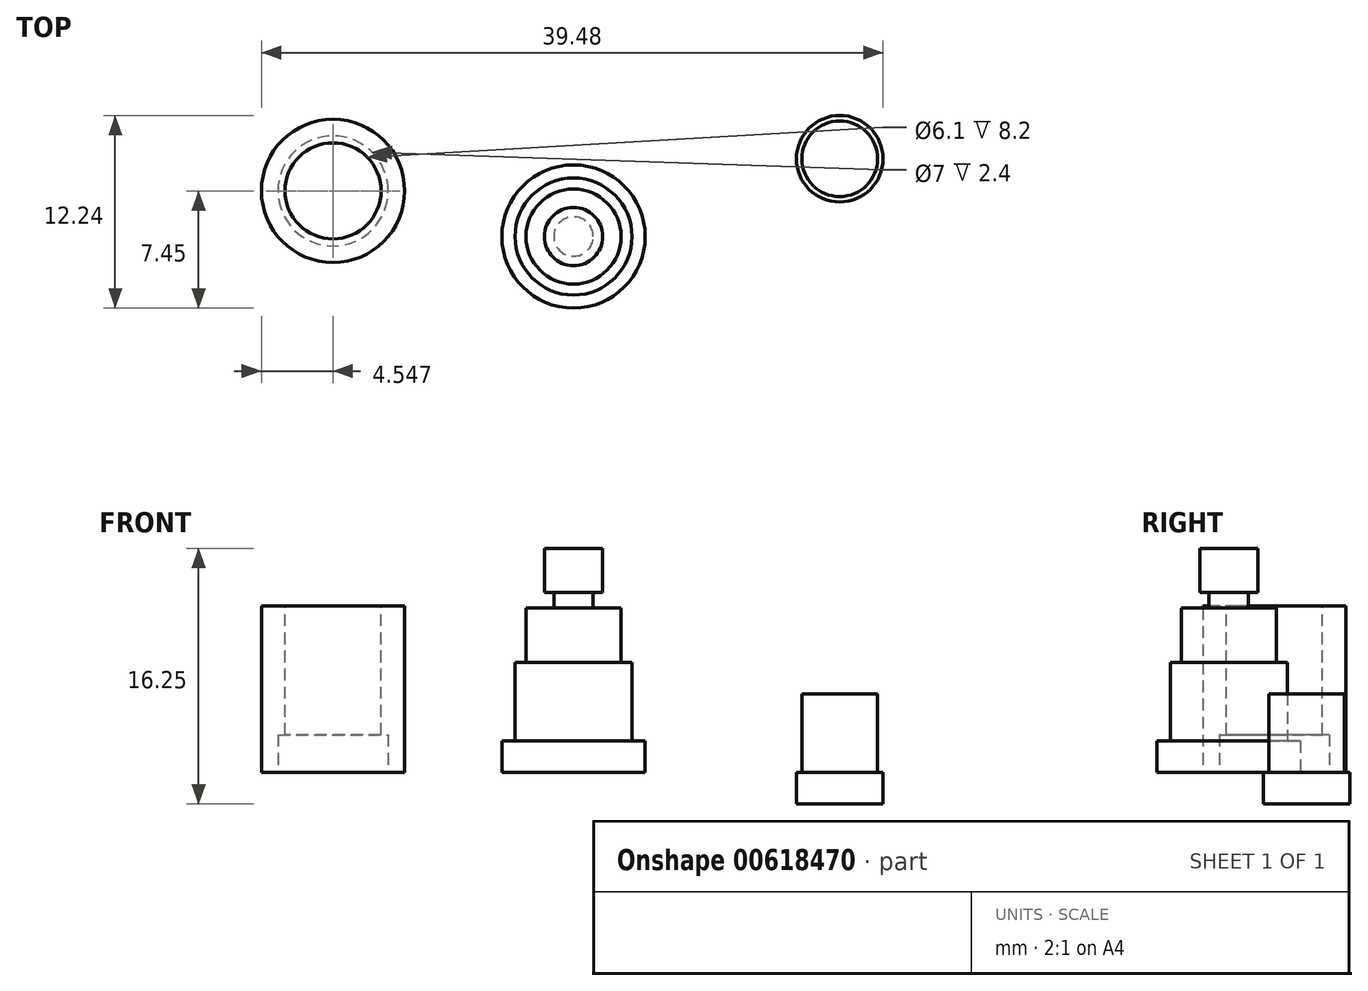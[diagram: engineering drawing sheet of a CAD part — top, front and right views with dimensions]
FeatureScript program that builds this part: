
annotation { "Feature Type Name" : "Feature", "Feature Type Description" : "" }
export const myFeature = defineFeature(function(context is Context, id is Id, definition is map)
    precondition{}
    {
        {
            var Q0;
            Q0=qCreatedBy(makeId("Top.planeOp"),FACE);
            var sketch = newSketch(context, id + "F0", { "sketchPlane" : qUnion([Q0])});
            skCircle(sketch, "E0", {"center": v(0, 0) * mm, "radius": 4.55 * mm});
            skSolve(sketch);
        }
        {
            var Q0;
            Q0=qCreatedBy(makeId("Top.planeOp"),FACE);
            var sketch = newSketch(context, id + "F1", { "sketchPlane" : qUnion([Q0])});
            skCircle(sketch, "E1", {"center": v(-15.27, 2.9) * mm, "radius": 4.55 * mm});
            skSolve(sketch);
        }
        {
            var Q0;
            Q0 = qSketchRegion(id + "F0", true);
            extrude(context, id + "F2", {"entities" : qUnion([Q0]), "depth" : 2 * mm, "offsetDistance" : 25 * mm});
        }
        {
            var Q0;
            Q0=makeQuery(id+"F2.opExtrude","CAP_FACE",FACE,{"disambiguationData":[OSD([sQuery(id+"F0.wireOp",EDGE,"E0")])],"isStart":false});
            var sketch = newSketch(context, id + "F3", { "sketchPlane" : qUnion([Q0])});
            skCircle(sketch, "E2", {"center": v(0, 0) * mm, "radius": 3.71 * mm});
            skSolve(sketch);
        }
        {
            var Q0;
            Q0=makeQuery(id+"F3.imprint","IMPRINT",FACE,{"disambiguationData":[TD([[makeQuery(id+"F3.imprint","IMPRINT",EDGE,{"derivedFrom":sQuery(id+"F3.wireOp",EDGE,"E2")}),1.0]])]});
            extrude(context, id + "F4", {"entities" : qUnion([Q0]), "operationType" : NewBodyOperationType.ADD, "depth" : 5 * mm, "offsetDistance" : 25 * mm});
        }
        {
            var Q0;
            Q0=makeQuery(id+"F4.opExtrude","CAP_FACE",FACE,{"disambiguationData":[OSD([sQuery(id+"F3.wireOp",EDGE,"E2")])],"isStart":false});
            var sketch = newSketch(context, id + "F5", { "sketchPlane" : qUnion([Q0])});
            skCircle(sketch, "E3", {"center": v(0, 0) * mm, "radius": 3.02 * mm});
            skSolve(sketch);
        }
        {
            var Q0;
            Q0=makeQuery(id+"F5.imprint","IMPRINT",FACE,{"disambiguationData":[TD([[makeQuery(id+"F5.imprint","IMPRINT",EDGE,{"derivedFrom":sQuery(id+"F5.wireOp",EDGE,"E3")}),1.0]])]});
            extrude(context, id + "F6", {"entities" : qUnion([Q0]), "operationType" : NewBodyOperationType.ADD, "depth" : 3.45 * mm, "offsetDistance" : 25 * mm});
        }
        {
            var Q0;
            Q0=makeQuery(id+"F6.opExtrude","CAP_FACE",FACE,{"disambiguationData":[OSD([sQuery(id+"F5.wireOp",EDGE,"E3")])],"isStart":false});
            var sketch = newSketch(context, id + "F7", { "sketchPlane" : qUnion([Q0])});
            skCircle(sketch, "E4", {"center": v(0, 0) * mm, "radius": 1.25 * mm});
            skSolve(sketch);
        }
        {
            var Q0;
            Q0=makeQuery(id+"F7.imprint","IMPRINT",FACE,{"disambiguationData":[TD([[makeQuery(id+"F7.imprint","IMPRINT",EDGE,{"derivedFrom":sQuery(id+"F7.wireOp",EDGE,"E4")}),1.0]])]});
            extrude(context, id + "F8", {"entities" : qUnion([Q0]), "operationType" : NewBodyOperationType.ADD, "depth" : 1 * mm, "offsetDistance" : 25 * mm});
        }
        {
            var Q0;
            Q0=makeQuery(id+"F8.opExtrude","CAP_FACE",FACE,{"disambiguationData":[OSD([sQuery(id+"F7.wireOp",EDGE,"E4")])],"isStart":false});
            var sketch = newSketch(context, id + "F9", { "sketchPlane" : qUnion([Q0])});
            skCircle(sketch, "E5", {"center": v(0, 0) * mm, "radius": 1.85 * mm});
            skSolve(sketch);
        }
        {
            var Q0;
            Q0=makeQuery(id+"F9.imprint","IMPRINT",FACE,{"disambiguationData":[TD([[makeQuery(id+"F9.imprint","IMPRINT",EDGE,{"derivedFrom":makeQuery(id+"F8.opExtrude","CAP_EDGE",EDGE,{"disambiguationData":[OSD([sQuery(id+"F7.wireOp",EDGE,"E4")])],"isStart":false})}),1.0]])]});
            var Q1;
            Q1=makeQuery(id+"F9.imprint","IMPRINT",FACE,{"disambiguationData":[TD([[makeQuery(id+"F9.imprint","IMPRINT",EDGE,{"derivedFrom":sQuery(id+"F9.wireOp",EDGE,"E5")}),1.0]])]});
            extrude(context, id + "F10", {"entities" : qUnion([Q0, Q1]), "operationType" : NewBodyOperationType.ADD, "depth" : 2.8 * mm, "offsetDistance" : 25 * mm});
        }
        {
            var Q0;
            Q0 = qSketchRegion(id + "F1", true);
            extrude(context, id + "F11", {"entities" : qUnion([Q0]), "depth" : 10.6 * mm, "offsetDistance" : 25 * mm});
        }
        {
            var Q0;
            Q0=makeQuery(id+"F11.opExtrude","CAP_FACE",FACE,{"disambiguationData":[OSD([sQuery(id+"F1.wireOp",EDGE,"E1")])],"isStart":false});
            var sketch = newSketch(context, id + "F12", { "sketchPlane" : qUnion([Q0])});
            skCircle(sketch, "E6", {"center": v(-15.27, 2.9) * mm, "radius": 3.05 * mm});
            skSolve(sketch);
        }
        {
            var Q0;
            Q0=makeQuery(id+"F12.imprint","IMPRINT",FACE,{"disambiguationData":[TD([[makeQuery(id+"F12.imprint","IMPRINT",EDGE,{"derivedFrom":sQuery(id+"F12.wireOp",EDGE,"E6")}),1.0]])]});
            extrude(context, id + "F13", {"entities" : qUnion([Q0]), "operationType" : NewBodyOperationType.REMOVE, "oppositeDirection" : true, "depth" : 8.2 * mm, "offsetDistance" : 25 * mm});
        }
        {
            var Q0;
            Q0=makeQuery(id+"F11.opExtrude","CAP_FACE",FACE,{"disambiguationData":[OSD([sQuery(id+"F1.wireOp",EDGE,"E1")])],"isStart":true});
            var sketch = newSketch(context, id + "F14", { "sketchPlane" : qUnion([Q0])});
            skCircle(sketch, "E7", {"center": v(-15.27, -2.9) * mm, "radius": 3.5 * mm});
            skSolve(sketch);
        }
        {
            var Q0;
            Q0=makeQuery(id+"F14.imprint","IMPRINT",FACE,{"disambiguationData":[TD([[makeQuery(id+"F14.imprint","IMPRINT",EDGE,{"derivedFrom":sQuery(id+"F14.wireOp",EDGE,"E7")}),1.0]])]});
            extrude(context, id + "F15", {"entities" : qUnion([Q0]), "operationType" : NewBodyOperationType.REMOVE, "oppositeDirection" : true, "depth" : 2.4 * mm, "offsetDistance" : 25 * mm});
        }
        {
            var Q0;
            Q0=qCreatedBy(makeId("Top.planeOp"),FACE);
            var sketch = newSketch(context, id + "F16", { "sketchPlane" : qUnion([Q0])});
            skCircle(sketch, "E8", {"center": v(16.9, 4.94) * mm, "radius": 2.4 * mm});
            skSolve(sketch);
        }
        {
            var Q0;
            Q0=makeQuery(id+"F16.imprint","IMPRINT",FACE,{"disambiguationData":[TD([[makeQuery(id+"F16.imprint","IMPRINT",EDGE,{"derivedFrom":sQuery(id+"F16.wireOp",EDGE,"E8")}),1.0]])]});
            extrude(context, id + "F17", {"entities" : qUnion([Q0]), "depth" : 5 * mm, "offsetDistance" : 25 * mm});
        }
        {
            var Q0;
            Q0=makeQuery(id+"F17.opExtrude","CAP_FACE",FACE,{"disambiguationData":[OSD([sQuery(id+"F16.wireOp",EDGE,"E8")])],"isStart":true});
            var sketch = newSketch(context, id + "F18", { "sketchPlane" : qUnion([Q0])});
            skCircle(sketch, "E9", {"center": v(16.9, -4.94) * mm, "radius": 2.75 * mm});
            skSolve(sketch);
        }
        {
            var Q0;
            Q0=makeQuery(id+"F18.imprint","IMPRINT",FACE,{"disambiguationData":[TD([[makeQuery(id+"F18.imprint","IMPRINT",EDGE,{"derivedFrom":makeQuery(id+"F17.opExtrude","CAP_EDGE",EDGE,{"disambiguationData":[OSD([sQuery(id+"F16.wireOp",EDGE,"E8")])],"isStart":true})}),-1.0]])]});
            var Q1;
            Q1=makeQuery(id+"F18.imprint","IMPRINT",FACE,{"disambiguationData":[TD([[makeQuery(id+"F18.imprint","IMPRINT",EDGE,{"derivedFrom":sQuery(id+"F18.wireOp",EDGE,"E9")}),1.0]])]});
            extrude(context, id + "F19", {"entities" : qUnion([Q0, Q1]), "operationType" : NewBodyOperationType.ADD, "depth" : 2 * mm, "offsetDistance" : 25 * mm});
        }
    });
